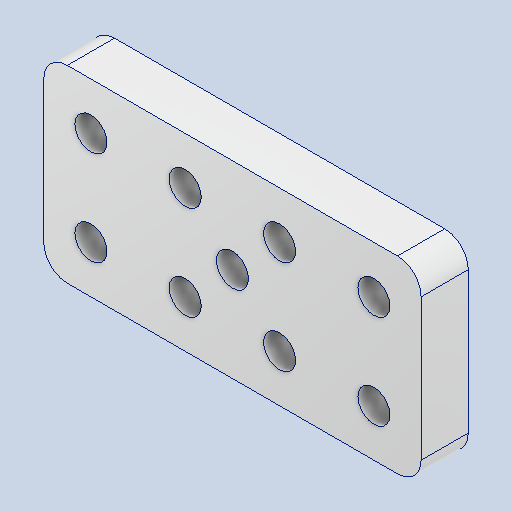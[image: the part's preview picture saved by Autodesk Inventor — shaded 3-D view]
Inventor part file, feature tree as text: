
AUTODESK INVENTOR PART (.ipt)
format: ipt  version: 2023 (Build 270158000, 158)  size: 154,112 bytes
history: native  units: in
note: dims shown in document units (in); Inventor stores cm internally (conversion verified against a paired STEP export)
features: other x3, sketch x1
ambient origin geometry x8: Origin, YZ Plane, XZ Plane, XY Plane, X Axis, Y Axis, Z Axis, Center Point
bodies: Solid1 (feature_tree)
feature tree (4):
  other  "IntakeShoulder.ipt"
  other  "Solid1::IntakeShoulder.ipt"
  other  "TaggingFeature1"
  sketch  "Sketch1"  dims[d0=0.3937in]
